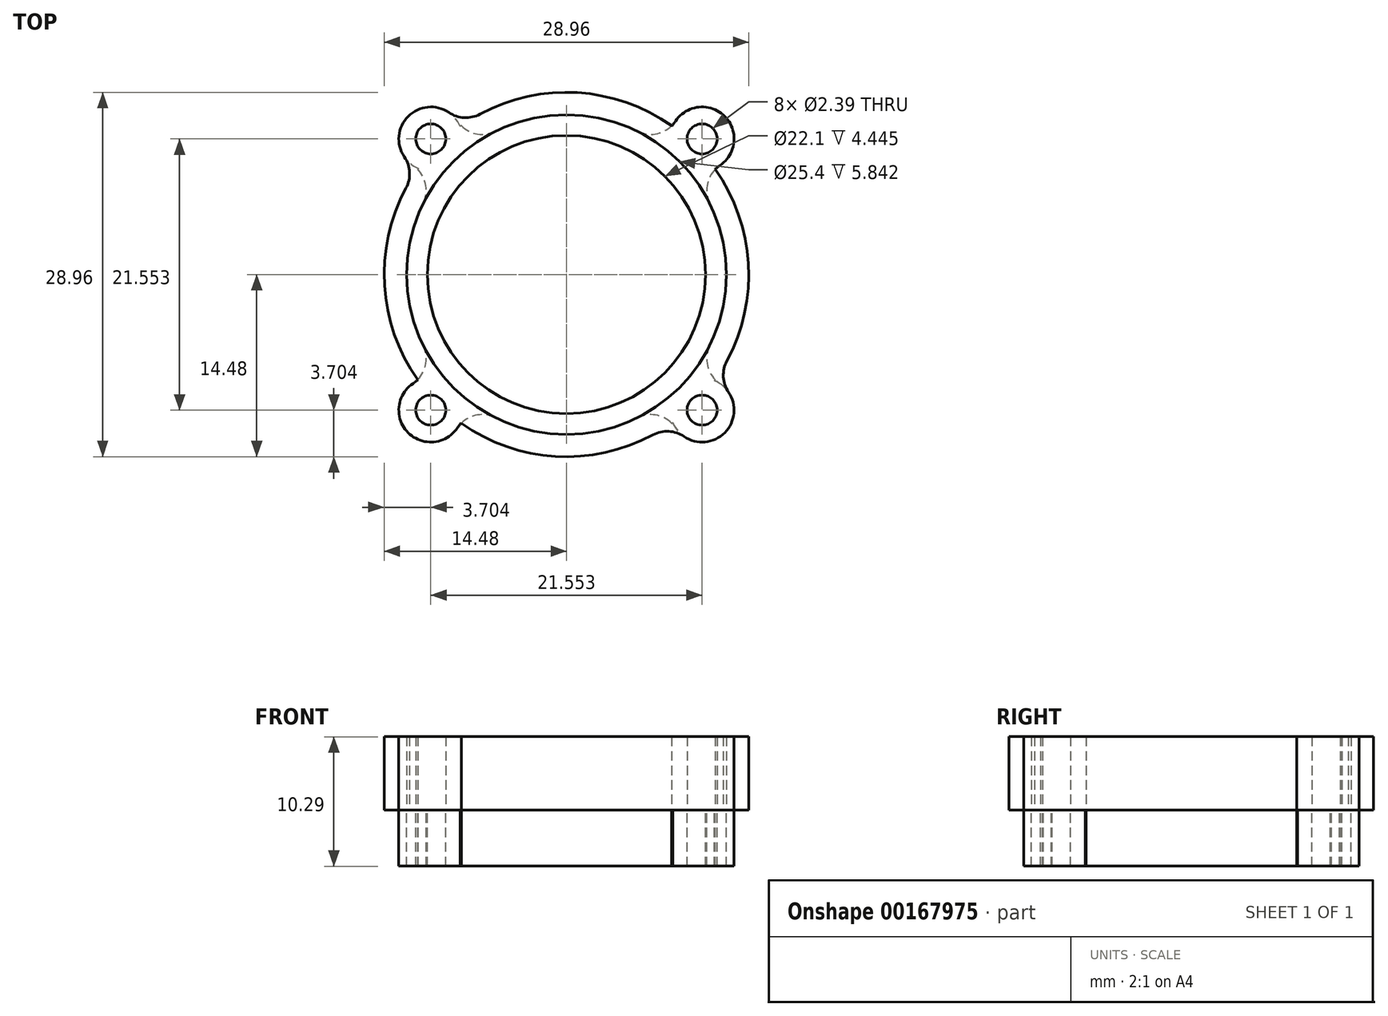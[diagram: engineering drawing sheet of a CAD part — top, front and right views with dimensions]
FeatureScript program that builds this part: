
annotation { "Feature Type Name" : "Feature", "Feature Type Description" : "" }
export const myFeature = defineFeature(function(context is Context, id is Id, definition is map)
    precondition{}
    {
        {
            var Q0;
            Q0=qCreatedBy(makeId("Top.planeOp"),FACE);
            var sketch = newSketch(context, id + "F0", { "sketchPlane" : qUnion([Q0])});
            skCircle(sketch, "E0", {"center": v(0, 0) * mm, "radius": 11.05 * mm});
            skCircle(sketch, "E1", {"center": v(0, 0) * mm, "radius": 12.7 * mm});
            skCircle(sketch, "E2", {"center": v(0, 0) * mm, "radius": 14.48 * mm});
            skCircle(sketch, "E3", {"center": v(-10.78, 10.78) * mm, "radius": 1.2 * mm});
            skCircle(sketch, "E4", {"center": v(-10.78, -10.78) * mm, "radius": 1.2 * mm});
            skCircle(sketch, "E5", {"center": v(10.78, 10.78) * mm, "radius": 1.2 * mm});
            skCircle(sketch, "E6", {"center": v(10.78, -10.78) * mm, "radius": 1.2 * mm});
            skLineSegment(sketch, "E7.bottom", {"start": v(-10.78, 10.78) * mm, "end": v(10.78, 10.78) * mm, "construction": true});
            skLineSegment(sketch, "E7.top", {"start": v(-10.78, -10.78) * mm, "end": v(10.78, -10.78) * mm, "construction": true});
            skLineSegment(sketch, "E7.left", {"start": v(-10.78, 10.78) * mm, "end": v(-10.78, -10.78) * mm, "construction": true});
            skLineSegment(sketch, "E7.right", {"start": v(10.78, 10.78) * mm, "end": v(10.78, -10.78) * mm, "construction": true});
            skArc(sketch, "E8", {"start": v(-8.44, 11.77) * mm, "mid": v(-12.57, 12.57) * mm, "end": v(-11.77, 8.44) * mm});
            skArc(sketch, "E9", {"start": v(8.44, -11.77) * mm, "mid": v(12.57, -12.57) * mm, "end": v(11.77, -8.44) * mm});
            skArc(sketch, "E10", {"start": v(-11.77, -8.44) * mm, "mid": v(-12.57, -12.57) * mm, "end": v(-8.44, -11.77) * mm});
            skArc(sketch, "E11", {"start": v(-11.38, 5.63) * mm, "mid": v(-11.22, 7.3) * mm, "end": v(-12.2, 8.67) * mm});
            skArc(sketch, "E12", {"start": v(-12.75, 6.87) * mm, "mid": v(-12.46, 8.12) * mm, "end": v(-12.87, 9.35) * mm});
            skArc(sketch, "E13", {"start": v(-9.35, 12.87) * mm, "mid": v(-8.12, 12.46) * mm, "end": v(-6.87, 12.75) * mm});
            skArc(sketch, "E14", {"start": v(-8.67, 12.2) * mm, "mid": v(-7.3, 11.22) * mm, "end": v(-5.63, 11.38) * mm});
            skArc(sketch, "E15.MirrorCS", {"start": v(11.38, 5.63) * mm, "mid": v(11.22, 7.3) * mm, "end": v(12.2, 8.67) * mm});
            skArc(sketch, "E16.MirrorCS", {"start": v(12.75, 6.87) * mm, "mid": v(12.46, 8.12) * mm, "end": v(12.87, 9.35) * mm});
            skArc(sketch, "E17.MirrorCS", {"start": v(9.35, 12.87) * mm, "mid": v(8.12, 12.46) * mm, "end": v(6.87, 12.75) * mm});
            skArc(sketch, "E18.MirrorCS", {"start": v(8.67, 12.2) * mm, "mid": v(7.3, 11.22) * mm, "end": v(5.63, 11.38) * mm});
            skArc(sketch, "E19.MirrorCS", {"start": v(-11.38, -5.63) * mm, "mid": v(-11.22, -7.3) * mm, "end": v(-12.2, -8.67) * mm});
            skArc(sketch, "E20.MirrorCS", {"start": v(-12.75, -6.87) * mm, "mid": v(-12.46, -8.12) * mm, "end": v(-12.87, -9.35) * mm});
            skArc(sketch, "E21.MirrorCS", {"start": v(-8.67, -12.2) * mm, "mid": v(-7.3, -11.22) * mm, "end": v(-5.63, -11.38) * mm});
            skArc(sketch, "E22.MirrorCS", {"start": v(-9.35, -12.87) * mm, "mid": v(-8.12, -12.46) * mm, "end": v(-6.87, -12.75) * mm});
            skArc(sketch, "E23.MirrorCS", {"start": v(8.67, -12.2) * mm, "mid": v(7.3, -11.22) * mm, "end": v(5.63, -11.38) * mm});
            skArc(sketch, "E24.MirrorCS", {"start": v(9.35, -12.87) * mm, "mid": v(8.12, -12.46) * mm, "end": v(6.87, -12.75) * mm});
            skArc(sketch, "E25.MirrorCS", {"start": v(12.75, -6.87) * mm, "mid": v(12.46, -8.12) * mm, "end": v(12.87, -9.35) * mm});
            skArc(sketch, "E26.MirrorCS", {"start": v(11.38, -5.63) * mm, "mid": v(11.22, -7.3) * mm, "end": v(12.2, -8.67) * mm});
            skArc(sketch, "E27.trimOffspring", {"start": v(11.77, 8.44) * mm, "mid": v(12.57, 12.57) * mm, "end": v(8.44, 11.77) * mm});
            skLineSegment(sketch, "E28", {"start": v(-12.87, 9.35) * mm, "end": v(-18.33, 14.8) * mm});
            skLineSegment(sketch, "E29", {"start": v(-18.33, 14.8) * mm, "end": v(-14.8, 18.33) * mm});
            skLineSegment(sketch, "E30", {"start": v(-14.8, 18.33) * mm, "end": v(-9.35, 12.87) * mm});
            skPoint(sketch, "E31", {"position": v(-16.56, 16.56) * mm});
            skArc(sketch, "E32", {"start": v(-14.8, 18.33) * mm, "mid": v(-18.33, 18.33) * mm, "end": v(-18.33, 14.8) * mm});
            skLineSegment(sketch, "E33", {"start": v(-16.56, 16.56) * mm, "end": v(-10.78, 10.78) * mm, "construction": true});
            skLineSegment(sketch, "E34", {"start": v(-9.35, 12.87) * mm, "end": v(-12.87, 9.35) * mm});
            skCircle(sketch, "E35", {"center": v(-16.56, 16.56) * mm, "radius": 1.2 * mm});
            skSolve(sketch);
        }
        {
            var Q0;
            {var subQ5=sQuery(id+"F0.wireOp",EDGE,"E11");var subQ7=sQuery(id+"F0.wireOp",EDGE,"E1");var subQ9=makeQuery(id+"F0.imprint","INTERSECT",VERTEX,{"derivedFrom":[subQ7,subQ5]});Q0=makeQuery(id+"F0.imprint","IMPRINT",FACE,{"disambiguationData":[TD([[makeQuery(id+"F0.imprint","IMPRINT",EDGE,{"disambiguationData":[TD([[subQ9,-1.0]])],"derivedFrom":subQ7}),-1.0]])]});}
            var Q1;
            {var subQ0=sQuery(id+"F0.wireOp",EDGE,"E12");Q1=makeQuery(id+"F0.imprint","IMPRINT",FACE,{"disambiguationData":[TD([[makeQuery(id+"F0.imprint","IMPRINT",EDGE,{"derivedFrom":subQ0}),-1.0]])]});}
            var Q2;
            {var subQ4=sQuery(id+"F0.wireOp",EDGE,"E14");var subQ5=sQuery(id+"F0.wireOp",EDGE,"E1");var subQ6=makeQuery(id+"F0.imprint","INTERSECT",VERTEX,{"derivedFrom":[subQ5,subQ4]});Q2=makeQuery(id+"F0.imprint","IMPRINT",FACE,{"disambiguationData":[TD([[makeQuery(id+"F0.imprint","IMPRINT",EDGE,{"disambiguationData":[TD([[subQ6,1.0]])],"derivedFrom":subQ5}),-1.0]])]});}
            var Q3;
            {var subQ5=sQuery(id+"F0.wireOp",EDGE,"E15.MirrorCS");var subQ7=sQuery(id+"F0.wireOp",EDGE,"E1");var subQ8=makeQuery(id+"F0.imprint","INTERSECT",VERTEX,{"derivedFrom":[subQ7,subQ5]});Q3=makeQuery(id+"F0.imprint","IMPRINT",FACE,{"disambiguationData":[TD([[makeQuery(id+"F0.imprint","IMPRINT",EDGE,{"disambiguationData":[TD([[subQ8,1.0]])],"derivedFrom":subQ7}),-1.0]])]});}
            var Q4;
            {var subQ0=sQuery(id+"F0.wireOp",EDGE,"E10");var subQ1=sQuery(id+"F0.wireOp",EDGE,"E2");var subQ2=makeQuery(id+"F0.imprint","INTERSECT",VERTEX,{"disambiguationData":[OD(0.0)],"derivedFrom":[subQ1,subQ0]});Q4=makeQuery(id+"F0.imprint","IMPRINT",FACE,{"disambiguationData":[TD([[makeQuery(id+"F0.imprint","IMPRINT",EDGE,{"disambiguationData":[TD([[subQ2,-1.0]])],"derivedFrom":subQ1}),-1.0]])]});}
            var Q5;
            {var subQ4=sQuery(id+"F0.wireOp",EDGE,"E1");var subQ7=sQuery(id+"F0.wireOp",EDGE,"E21.MirrorCS");var subQ9=makeQuery(id+"F0.imprint","INTERSECT",VERTEX,{"derivedFrom":[subQ4,subQ7]});Q5=makeQuery(id+"F0.imprint","IMPRINT",FACE,{"disambiguationData":[TD([[makeQuery(id+"F0.imprint","IMPRINT",EDGE,{"disambiguationData":[TD([[subQ9,-1.0]])],"derivedFrom":subQ4}),-1.0]])]});}
            var Q6;
            {var subQ0=sQuery(id+"F0.wireOp",EDGE,"E24.MirrorCS");Q6=makeQuery(id+"F0.imprint","IMPRINT",FACE,{"disambiguationData":[TD([[makeQuery(id+"F0.imprint","IMPRINT",EDGE,{"derivedFrom":subQ0}),-1.0]])]});}
            var Q7;
            {var subQ0=sQuery(id+"F0.wireOp",EDGE,"E22.MirrorCS");Q7=makeQuery(id+"F0.imprint","IMPRINT",FACE,{"disambiguationData":[TD([[makeQuery(id+"F0.imprint","IMPRINT",EDGE,{"derivedFrom":subQ0}),1.0]])]});}
            var Q8;
            {var subQ9=sQuery(id+"F0.wireOp",EDGE,"E23.MirrorCS");var subQ11=sQuery(id+"F0.wireOp",EDGE,"E1");var subQ12=makeQuery(id+"F0.imprint","INTERSECT",VERTEX,{"derivedFrom":[subQ11,subQ9]});Q8=makeQuery(id+"F0.imprint","IMPRINT",FACE,{"disambiguationData":[TD([[makeQuery(id+"F0.imprint","IMPRINT",EDGE,{"disambiguationData":[TD([[subQ12,-1.0]])],"derivedFrom":subQ11}),-1.0]])]});}
            var Q9;
            {var subQ9=sQuery(id+"F0.wireOp",EDGE,"E23.MirrorCS");var subQ11=sQuery(id+"F0.wireOp",EDGE,"E1");var subQ12=makeQuery(id+"F0.imprint","INTERSECT",VERTEX,{"derivedFrom":[subQ11,subQ9]});Q9=makeQuery(id+"F0.imprint","IMPRINT",FACE,{"disambiguationData":[TD([[makeQuery(id+"F0.imprint","IMPRINT",EDGE,{"disambiguationData":[TD([[subQ12,-1.0]])],"derivedFrom":subQ11}),-1.0]])]});}
            var Q10;
            {var subQ5=sQuery(id+"F0.wireOp",EDGE,"E19.MirrorCS");var subQ6=sQuery(id+"F0.wireOp",EDGE,"E1");var subQ7=makeQuery(id+"F0.imprint","INTERSECT",VERTEX,{"derivedFrom":[subQ6,subQ5]});Q10=makeQuery(id+"F0.imprint","IMPRINT",FACE,{"disambiguationData":[TD([[makeQuery(id+"F0.imprint","IMPRINT",EDGE,{"disambiguationData":[TD([[subQ7,-1.0]])],"derivedFrom":subQ6}),-1.0]])]});}
            var Q11;
            {var subQ5=sQuery(id+"F0.wireOp",EDGE,"E19.MirrorCS");var subQ6=sQuery(id+"F0.wireOp",EDGE,"E1");var subQ7=makeQuery(id+"F0.imprint","INTERSECT",VERTEX,{"derivedFrom":[subQ6,subQ5]});Q11=makeQuery(id+"F0.imprint","IMPRINT",FACE,{"disambiguationData":[TD([[makeQuery(id+"F0.imprint","IMPRINT",EDGE,{"disambiguationData":[TD([[subQ7,-1.0]])],"derivedFrom":subQ6}),-1.0]])]});}
            var Q12;
            {var subQ5=sQuery(id+"F0.wireOp",EDGE,"E19.MirrorCS");var subQ6=sQuery(id+"F0.wireOp",EDGE,"E1");var subQ7=makeQuery(id+"F0.imprint","INTERSECT",VERTEX,{"derivedFrom":[subQ6,subQ5]});Q12=makeQuery(id+"F0.imprint","IMPRINT",FACE,{"disambiguationData":[TD([[makeQuery(id+"F0.imprint","IMPRINT",EDGE,{"disambiguationData":[TD([[subQ7,-1.0]])],"derivedFrom":subQ6}),-1.0]])]});}
            var Q13;
            {var subQ9=sQuery(id+"F0.wireOp",EDGE,"E11");var subQ10=sQuery(id+"F0.wireOp",EDGE,"E1");var subQ11=makeQuery(id+"F0.imprint","INTERSECT",VERTEX,{"derivedFrom":[subQ10,subQ9]});Q13=makeQuery(id+"F0.imprint","IMPRINT",FACE,{"disambiguationData":[TD([[makeQuery(id+"F0.imprint","IMPRINT",EDGE,{"disambiguationData":[TD([[subQ11,1.0]])],"derivedFrom":subQ10}),-1.0]])]});}
            var Q14;
            {var subQ9=sQuery(id+"F0.wireOp",EDGE,"E11");var subQ10=sQuery(id+"F0.wireOp",EDGE,"E1");var subQ11=makeQuery(id+"F0.imprint","INTERSECT",VERTEX,{"derivedFrom":[subQ10,subQ9]});Q14=makeQuery(id+"F0.imprint","IMPRINT",FACE,{"disambiguationData":[TD([[makeQuery(id+"F0.imprint","IMPRINT",EDGE,{"disambiguationData":[TD([[subQ11,1.0]])],"derivedFrom":subQ10}),-1.0]])]});}
            var Q15;
            {var subQ9=sQuery(id+"F0.wireOp",EDGE,"E11");var subQ10=sQuery(id+"F0.wireOp",EDGE,"E1");var subQ11=makeQuery(id+"F0.imprint","INTERSECT",VERTEX,{"derivedFrom":[subQ10,subQ9]});Q15=makeQuery(id+"F0.imprint","IMPRINT",FACE,{"disambiguationData":[TD([[makeQuery(id+"F0.imprint","IMPRINT",EDGE,{"disambiguationData":[TD([[subQ11,1.0]])],"derivedFrom":subQ10}),-1.0]])]});}
            var Q16;
            {var subQ7=sQuery(id+"F0.wireOp",EDGE,"E15.MirrorCS");var subQ8=sQuery(id+"F0.wireOp",EDGE,"E1");var subQ9=makeQuery(id+"F0.imprint","INTERSECT",VERTEX,{"derivedFrom":[subQ8,subQ7]});Q16=makeQuery(id+"F0.imprint","IMPRINT",FACE,{"disambiguationData":[TD([[makeQuery(id+"F0.imprint","IMPRINT",EDGE,{"disambiguationData":[TD([[subQ9,-1.0]])],"derivedFrom":subQ8}),-1.0]])]});}
            var Q17;
            {var subQ0=sQuery(id+"F0.wireOp",EDGE,"E25.MirrorCS");Q17=makeQuery(id+"F0.imprint","IMPRINT",FACE,{"disambiguationData":[TD([[makeQuery(id+"F0.imprint","IMPRINT",EDGE,{"derivedFrom":subQ0}),-1.0]])]});}
            var Q18;
            {var subQ0=sQuery(id+"F0.wireOp",EDGE,"E9");var subQ1=sQuery(id+"F0.wireOp",EDGE,"E2");var subQ2=makeQuery(id+"F0.imprint","INTERSECT",VERTEX,{"disambiguationData":[OD(1.0)],"derivedFrom":[subQ1,subQ0]});Q18=makeQuery(id+"F0.imprint","IMPRINT",FACE,{"disambiguationData":[TD([[makeQuery(id+"F0.imprint","IMPRINT",EDGE,{"disambiguationData":[TD([[subQ2,-1.0]])],"derivedFrom":subQ1}),-1.0]])]});}
            var Q19;
            {var subQ0=sQuery(id+"F0.wireOp",EDGE,"E9");var subQ1=sQuery(id+"F0.wireOp",EDGE,"E2");var subQ2=makeQuery(id+"F0.imprint","INTERSECT",VERTEX,{"disambiguationData":[OD(0.0)],"derivedFrom":[subQ1,subQ0]});Q19=makeQuery(id+"F0.imprint","IMPRINT",FACE,{"disambiguationData":[TD([[makeQuery(id+"F0.imprint","IMPRINT",EDGE,{"disambiguationData":[TD([[subQ2,1.0]])],"derivedFrom":subQ1}),-1.0]])]});}
            var Q20;
            {var subQ0=sQuery(id+"F0.wireOp",EDGE,"E9");var subQ1=sQuery(id+"F0.wireOp",EDGE,"E2");var subQ2=makeQuery(id+"F0.imprint","INTERSECT",VERTEX,{"disambiguationData":[OD(0.0)],"derivedFrom":[subQ1,subQ0]});Q20=makeQuery(id+"F0.imprint","IMPRINT",FACE,{"disambiguationData":[TD([[makeQuery(id+"F0.imprint","IMPRINT",EDGE,{"disambiguationData":[TD([[subQ2,-1.0]])],"derivedFrom":subQ1}),-1.0]])]});}
            var Q21;
            {var subQ0=sQuery(id+"F0.wireOp",EDGE,"E20.MirrorCS");Q21=makeQuery(id+"F0.imprint","IMPRINT",FACE,{"disambiguationData":[TD([[makeQuery(id+"F0.imprint","IMPRINT",EDGE,{"derivedFrom":subQ0}),1.0]])]});}
            var Q22;
            {var subQ0=sQuery(id+"F0.wireOp",EDGE,"E10");var subQ1=sQuery(id+"F0.wireOp",EDGE,"E2");var subQ2=makeQuery(id+"F0.imprint","INTERSECT",VERTEX,{"disambiguationData":[OD(0.0)],"derivedFrom":[subQ1,subQ0]});Q22=makeQuery(id+"F0.imprint","IMPRINT",FACE,{"disambiguationData":[TD([[makeQuery(id+"F0.imprint","IMPRINT",EDGE,{"disambiguationData":[TD([[subQ2,1.0]])],"derivedFrom":subQ1}),-1.0]])]});}
            var Q23;
            {var subQ0=sQuery(id+"F0.wireOp",EDGE,"E10");var subQ1=sQuery(id+"F0.wireOp",EDGE,"E2");var subQ2=makeQuery(id+"F0.imprint","INTERSECT",VERTEX,{"disambiguationData":[OD(1.0)],"derivedFrom":[subQ1,subQ0]});Q23=makeQuery(id+"F0.imprint","IMPRINT",FACE,{"disambiguationData":[TD([[makeQuery(id+"F0.imprint","IMPRINT",EDGE,{"disambiguationData":[TD([[subQ2,-1.0]])],"derivedFrom":subQ1}),-1.0]])]});}
            var Q24;
            {var subQ1=sQuery(id+"F0.wireOp",EDGE,"E2");var subQ5=sQuery(id+"F0.wireOp",EDGE,"E8");var subQ8=makeQuery(id+"F0.imprint","INTERSECT",VERTEX,{"disambiguationData":[OD(0.0)],"derivedFrom":[subQ1,subQ5]});Q24=makeQuery(id+"F0.imprint","IMPRINT",FACE,{"disambiguationData":[TD([[makeQuery(id+"F0.imprint","IMPRINT",EDGE,{"disambiguationData":[TD([[subQ8,-1.0]])],"derivedFrom":subQ1}),-1.0]])]});}
            var Q25;
            {var subQ0=sQuery(id+"F0.wireOp",EDGE,"E8");var subQ1=sQuery(id+"F0.wireOp",EDGE,"E2");var subQ2=makeQuery(id+"F0.imprint","INTERSECT",VERTEX,{"disambiguationData":[OD(0.0)],"derivedFrom":[subQ1,subQ0]});Q25=makeQuery(id+"F0.imprint","IMPRINT",FACE,{"disambiguationData":[TD([[makeQuery(id+"F0.imprint","IMPRINT",EDGE,{"disambiguationData":[TD([[subQ2,1.0]])],"derivedFrom":subQ1}),-1.0]])]});}
            var Q26;
            {var subQ0=sQuery(id+"F0.wireOp",EDGE,"E13");Q26=makeQuery(id+"F0.imprint","IMPRINT",FACE,{"disambiguationData":[TD([[makeQuery(id+"F0.imprint","IMPRINT",EDGE,{"derivedFrom":subQ0}),-1.0]])]});}
            var Q27;
            {var subQ0=sQuery(id+"F0.wireOp",EDGE,"E8");var subQ1=sQuery(id+"F0.wireOp",EDGE,"E2");var subQ2=makeQuery(id+"F0.imprint","INTERSECT",VERTEX,{"disambiguationData":[OD(1.0)],"derivedFrom":[subQ1,subQ0]});Q27=makeQuery(id+"F0.imprint","IMPRINT",FACE,{"disambiguationData":[TD([[makeQuery(id+"F0.imprint","IMPRINT",EDGE,{"disambiguationData":[TD([[subQ2,-1.0]])],"derivedFrom":subQ1}),-1.0]])]});}
            var Q28;
            {var subQ0=sQuery(id+"F0.wireOp",EDGE,"E17.MirrorCS");Q28=makeQuery(id+"F0.imprint","IMPRINT",FACE,{"disambiguationData":[TD([[makeQuery(id+"F0.imprint","IMPRINT",EDGE,{"derivedFrom":subQ0}),1.0]])]});}
            var Q29;
            {var subQ0=sQuery(id+"F0.wireOp",EDGE,"E27.trimOffspring");var subQ1=sQuery(id+"F0.wireOp",EDGE,"E2");var subQ2=makeQuery(id+"F0.imprint","INTERSECT",VERTEX,{"disambiguationData":[OD(1.0)],"derivedFrom":[subQ1,subQ0]});Q29=makeQuery(id+"F0.imprint","IMPRINT",FACE,{"disambiguationData":[TD([[makeQuery(id+"F0.imprint","IMPRINT",EDGE,{"disambiguationData":[TD([[subQ2,-1.0]])],"derivedFrom":subQ1}),-1.0]])]});}
            var Q30;
            {var subQ0=sQuery(id+"F0.wireOp",EDGE,"E8");var subQ1=sQuery(id+"F0.wireOp",EDGE,"E2");var subQ2=makeQuery(id+"F0.imprint","INTERSECT",VERTEX,{"disambiguationData":[OD(1.0)],"derivedFrom":[subQ1,subQ0]});Q30=makeQuery(id+"F0.imprint","IMPRINT",FACE,{"disambiguationData":[TD([[makeQuery(id+"F0.imprint","IMPRINT",EDGE,{"disambiguationData":[TD([[subQ2,-1.0]])],"derivedFrom":subQ1}),-1.0]])]});}
            var Q31;
            {var subQ0=sQuery(id+"F0.wireOp",EDGE,"E10");var subQ1=sQuery(id+"F0.wireOp",EDGE,"E2");var subQ2=makeQuery(id+"F0.imprint","INTERSECT",VERTEX,{"disambiguationData":[OD(1.0)],"derivedFrom":[subQ1,subQ0]});Q31=makeQuery(id+"F0.imprint","IMPRINT",FACE,{"disambiguationData":[TD([[makeQuery(id+"F0.imprint","IMPRINT",EDGE,{"disambiguationData":[TD([[subQ2,-1.0]])],"derivedFrom":subQ1}),-1.0]])]});}
            var Q32;
            {var subQ0=sQuery(id+"F0.wireOp",EDGE,"E9");var subQ1=sQuery(id+"F0.wireOp",EDGE,"E2");var subQ2=makeQuery(id+"F0.imprint","INTERSECT",VERTEX,{"disambiguationData":[OD(1.0)],"derivedFrom":[subQ1,subQ0]});Q32=makeQuery(id+"F0.imprint","IMPRINT",FACE,{"disambiguationData":[TD([[makeQuery(id+"F0.imprint","IMPRINT",EDGE,{"disambiguationData":[TD([[subQ2,-1.0]])],"derivedFrom":subQ1}),-1.0]])]});}
            var Q33;
            {var subQ0=sQuery(id+"F0.wireOp",EDGE,"E27.trimOffspring");var subQ1=sQuery(id+"F0.wireOp",EDGE,"E2");var subQ2=makeQuery(id+"F0.imprint","INTERSECT",VERTEX,{"disambiguationData":[OD(0.0)],"derivedFrom":[subQ1,subQ0]});Q33=makeQuery(id+"F0.imprint","IMPRINT",FACE,{"disambiguationData":[TD([[makeQuery(id+"F0.imprint","IMPRINT",EDGE,{"disambiguationData":[TD([[subQ2,1.0]])],"derivedFrom":subQ1}),-1.0]])]});}
            var Q34;
            {var subQ0=sQuery(id+"F0.wireOp",EDGE,"E16.MirrorCS");Q34=makeQuery(id+"F0.imprint","IMPRINT",FACE,{"disambiguationData":[TD([[makeQuery(id+"F0.imprint","IMPRINT",EDGE,{"derivedFrom":subQ0}),1.0]])]});}
            var Q35;
            {var subQ0=sQuery(id+"F0.wireOp",EDGE,"E34");var subQ1=sQuery(id+"F0.wireOp",EDGE,"E3");var subQ2=makeQuery(id+"F0.imprint","INTERSECT",VERTEX,{"disambiguationData":[OD(0.0)],"derivedFrom":[subQ1,subQ0]});Q35=makeQuery(id+"F0.imprint","IMPRINT",FACE,{"disambiguationData":[TD([[makeQuery(id+"F0.imprint","IMPRINT",EDGE,{"disambiguationData":[TD([[subQ2,-1.0]])],"derivedFrom":subQ1}),-1.0]])]});}
            var Q36;
            {var subQ0=sQuery(id+"F0.wireOp",EDGE,"E8");var subQ1=sQuery(id+"F0.wireOp",EDGE,"E2");var subQ2=makeQuery(id+"F0.imprint","INTERSECT",VERTEX,{"disambiguationData":[OD(1.0)],"derivedFrom":[subQ1,subQ0]});Q36=makeQuery(id+"F0.imprint","IMPRINT",FACE,{"disambiguationData":[TD([[makeQuery(id+"F0.imprint","IMPRINT",EDGE,{"disambiguationData":[TD([[subQ2,1.0]])],"derivedFrom":subQ1}),-1.0]])]});}
            var Q37;
            {var subQ1=sQuery(id+"F0.wireOp",EDGE,"E2");var subQ4=sQuery(id+"F0.wireOp",EDGE,"E27.trimOffspring");var subQ9=makeQuery(id+"F0.imprint","INTERSECT",VERTEX,{"disambiguationData":[OD(0.0)],"derivedFrom":[subQ1,subQ4]});Q37=makeQuery(id+"F0.imprint","IMPRINT",FACE,{"disambiguationData":[TD([[makeQuery(id+"F0.imprint","IMPRINT",EDGE,{"disambiguationData":[TD([[subQ9,-1.0]])],"derivedFrom":subQ1}),-1.0]])]});}
            extrude(context, id + "F1", {"entities" : qUnion([Q0, Q1, Q2, Q3, Q4, Q5, Q6, Q7, Q8, Q9, Q10, Q11, Q12, Q13, Q14, Q15, Q16, Q17, Q18, Q19, Q20, Q21, Q22, Q23, Q24, Q25, Q26, Q27, Q28, Q29, Q30, Q31, Q32, Q33, Q34, Q35, Q36, Q37]), "depth" : 5.84 * mm, "offsetDistance" : 25.4 * mm});
        }
        {
            var Q0;
            {var subQ1=sQuery(id+"F0.wireOp",EDGE,"E2");var subQ5=sQuery(id+"F0.wireOp",EDGE,"E8");var subQ8=makeQuery(id+"F0.imprint","INTERSECT",VERTEX,{"disambiguationData":[OD(0.0)],"derivedFrom":[subQ1,subQ5]});Q0=makeQuery(id+"F0.imprint","IMPRINT",FACE,{"disambiguationData":[TD([[makeQuery(id+"F0.imprint","IMPRINT",EDGE,{"disambiguationData":[TD([[subQ8,-1.0]])],"derivedFrom":subQ1}),-1.0]])]});}
            var Q1;
            {var subQ0=sQuery(id+"F0.wireOp",EDGE,"E10");var subQ1=sQuery(id+"F0.wireOp",EDGE,"E2");var subQ2=makeQuery(id+"F0.imprint","INTERSECT",VERTEX,{"disambiguationData":[OD(0.0)],"derivedFrom":[subQ1,subQ0]});Q1=makeQuery(id+"F0.imprint","IMPRINT",FACE,{"disambiguationData":[TD([[makeQuery(id+"F0.imprint","IMPRINT",EDGE,{"disambiguationData":[TD([[subQ2,-1.0]])],"derivedFrom":subQ1}),-1.0]])]});}
            var Q2;
            {var subQ0=sQuery(id+"F0.wireOp",EDGE,"E9");var subQ1=sQuery(id+"F0.wireOp",EDGE,"E2");var subQ2=makeQuery(id+"F0.imprint","INTERSECT",VERTEX,{"disambiguationData":[OD(0.0)],"derivedFrom":[subQ1,subQ0]});Q2=makeQuery(id+"F0.imprint","IMPRINT",FACE,{"disambiguationData":[TD([[makeQuery(id+"F0.imprint","IMPRINT",EDGE,{"disambiguationData":[TD([[subQ2,-1.0]])],"derivedFrom":subQ1}),-1.0]])]});}
            var Q3;
            Q3=makeQuery(id+"F0.imprint","IMPRINT",FACE,{"disambiguationData":[TD([[makeQuery(id+"F0.imprint","IMPRINT",EDGE,{"derivedFrom":sQuery(id+"F0.wireOp",EDGE,"E0")}),-1.0]])]});
            var Q4;
            {var subQ5=sQuery(id+"F0.wireOp",EDGE,"E19.MirrorCS");var subQ6=sQuery(id+"F0.wireOp",EDGE,"E1");var subQ7=makeQuery(id+"F0.imprint","INTERSECT",VERTEX,{"derivedFrom":[subQ6,subQ5]});Q4=makeQuery(id+"F0.imprint","IMPRINT",FACE,{"disambiguationData":[TD([[makeQuery(id+"F0.imprint","IMPRINT",EDGE,{"disambiguationData":[TD([[subQ7,-1.0]])],"derivedFrom":subQ6}),-1.0]])]});}
            var Q5;
            {var subQ5=sQuery(id+"F0.wireOp",EDGE,"E19.MirrorCS");var subQ6=sQuery(id+"F0.wireOp",EDGE,"E1");var subQ7=makeQuery(id+"F0.imprint","INTERSECT",VERTEX,{"derivedFrom":[subQ6,subQ5]});Q5=makeQuery(id+"F0.imprint","IMPRINT",FACE,{"disambiguationData":[TD([[makeQuery(id+"F0.imprint","IMPRINT",EDGE,{"disambiguationData":[TD([[subQ7,-1.0]])],"derivedFrom":subQ6}),-1.0]])]});}
            var Q6;
            {var subQ5=sQuery(id+"F0.wireOp",EDGE,"E19.MirrorCS");var subQ6=sQuery(id+"F0.wireOp",EDGE,"E1");var subQ7=makeQuery(id+"F0.imprint","INTERSECT",VERTEX,{"derivedFrom":[subQ6,subQ5]});Q6=makeQuery(id+"F0.imprint","IMPRINT",FACE,{"disambiguationData":[TD([[makeQuery(id+"F0.imprint","IMPRINT",EDGE,{"disambiguationData":[TD([[subQ7,-1.0]])],"derivedFrom":subQ6}),-1.0]])]});}
            var Q7;
            {var subQ7=sQuery(id+"F0.wireOp",EDGE,"E15.MirrorCS");var subQ8=sQuery(id+"F0.wireOp",EDGE,"E1");var subQ9=makeQuery(id+"F0.imprint","INTERSECT",VERTEX,{"derivedFrom":[subQ8,subQ7]});Q7=makeQuery(id+"F0.imprint","IMPRINT",FACE,{"disambiguationData":[TD([[makeQuery(id+"F0.imprint","IMPRINT",EDGE,{"disambiguationData":[TD([[subQ9,-1.0]])],"derivedFrom":subQ8}),-1.0]])]});}
            var Q8;
            {var subQ9=sQuery(id+"F0.wireOp",EDGE,"E23.MirrorCS");var subQ11=sQuery(id+"F0.wireOp",EDGE,"E1");var subQ12=makeQuery(id+"F0.imprint","INTERSECT",VERTEX,{"derivedFrom":[subQ11,subQ9]});Q8=makeQuery(id+"F0.imprint","IMPRINT",FACE,{"disambiguationData":[TD([[makeQuery(id+"F0.imprint","IMPRINT",EDGE,{"disambiguationData":[TD([[subQ12,-1.0]])],"derivedFrom":subQ11}),-1.0]])]});}
            var Q9;
            {var subQ9=sQuery(id+"F0.wireOp",EDGE,"E23.MirrorCS");var subQ11=sQuery(id+"F0.wireOp",EDGE,"E1");var subQ12=makeQuery(id+"F0.imprint","INTERSECT",VERTEX,{"derivedFrom":[subQ11,subQ9]});Q9=makeQuery(id+"F0.imprint","IMPRINT",FACE,{"disambiguationData":[TD([[makeQuery(id+"F0.imprint","IMPRINT",EDGE,{"disambiguationData":[TD([[subQ12,-1.0]])],"derivedFrom":subQ11}),-1.0]])]});}
            var Q10;
            {var subQ9=sQuery(id+"F0.wireOp",EDGE,"E23.MirrorCS");var subQ11=sQuery(id+"F0.wireOp",EDGE,"E1");var subQ12=makeQuery(id+"F0.imprint","INTERSECT",VERTEX,{"derivedFrom":[subQ11,subQ9]});Q10=makeQuery(id+"F0.imprint","IMPRINT",FACE,{"disambiguationData":[TD([[makeQuery(id+"F0.imprint","IMPRINT",EDGE,{"disambiguationData":[TD([[subQ12,-1.0]])],"derivedFrom":subQ11}),-1.0]])]});}
            var Q11;
            {var subQ9=sQuery(id+"F0.wireOp",EDGE,"E11");var subQ10=sQuery(id+"F0.wireOp",EDGE,"E1");var subQ11=makeQuery(id+"F0.imprint","INTERSECT",VERTEX,{"derivedFrom":[subQ10,subQ9]});Q11=makeQuery(id+"F0.imprint","IMPRINT",FACE,{"disambiguationData":[TD([[makeQuery(id+"F0.imprint","IMPRINT",EDGE,{"disambiguationData":[TD([[subQ11,1.0]])],"derivedFrom":subQ10}),-1.0]])]});}
            var Q12;
            {var subQ9=sQuery(id+"F0.wireOp",EDGE,"E11");var subQ10=sQuery(id+"F0.wireOp",EDGE,"E1");var subQ11=makeQuery(id+"F0.imprint","INTERSECT",VERTEX,{"derivedFrom":[subQ10,subQ9]});Q12=makeQuery(id+"F0.imprint","IMPRINT",FACE,{"disambiguationData":[TD([[makeQuery(id+"F0.imprint","IMPRINT",EDGE,{"disambiguationData":[TD([[subQ11,1.0]])],"derivedFrom":subQ10}),-1.0]])]});}
            var Q13;
            {var subQ0=sQuery(id+"F0.wireOp",EDGE,"E34");var subQ1=sQuery(id+"F0.wireOp",EDGE,"E3");var subQ2=makeQuery(id+"F0.imprint","INTERSECT",VERTEX,{"disambiguationData":[OD(0.0)],"derivedFrom":[subQ1,subQ0]});Q13=makeQuery(id+"F0.imprint","IMPRINT",FACE,{"disambiguationData":[TD([[makeQuery(id+"F0.imprint","IMPRINT",EDGE,{"disambiguationData":[TD([[subQ2,-1.0]])],"derivedFrom":subQ1}),-1.0]])]});}
            var Q14;
            {var subQ0=sQuery(id+"F0.wireOp",EDGE,"E8");var subQ1=sQuery(id+"F0.wireOp",EDGE,"E2");var subQ2=makeQuery(id+"F0.imprint","INTERSECT",VERTEX,{"disambiguationData":[OD(1.0)],"derivedFrom":[subQ1,subQ0]});Q14=makeQuery(id+"F0.imprint","IMPRINT",FACE,{"disambiguationData":[TD([[makeQuery(id+"F0.imprint","IMPRINT",EDGE,{"disambiguationData":[TD([[subQ2,1.0]])],"derivedFrom":subQ1}),-1.0]])]});}
            var Q15;
            {var subQ1=sQuery(id+"F0.wireOp",EDGE,"E2");var subQ4=sQuery(id+"F0.wireOp",EDGE,"E27.trimOffspring");var subQ9=makeQuery(id+"F0.imprint","INTERSECT",VERTEX,{"disambiguationData":[OD(0.0)],"derivedFrom":[subQ1,subQ4]});Q15=makeQuery(id+"F0.imprint","IMPRINT",FACE,{"disambiguationData":[TD([[makeQuery(id+"F0.imprint","IMPRINT",EDGE,{"disambiguationData":[TD([[subQ9,-1.0]])],"derivedFrom":subQ1}),-1.0]])]});}
            extrude(context, id + "F2", {"entities" : qUnion([Q0, Q1, Q2, Q3, Q4, Q5, Q6, Q7, Q8, Q9, Q10, Q11, Q12, Q13, Q14, Q15]), "oppositeDirection" : true, "depth" : 4.44 * mm, "offsetDistance" : 25.4 * mm});
        }
    });
